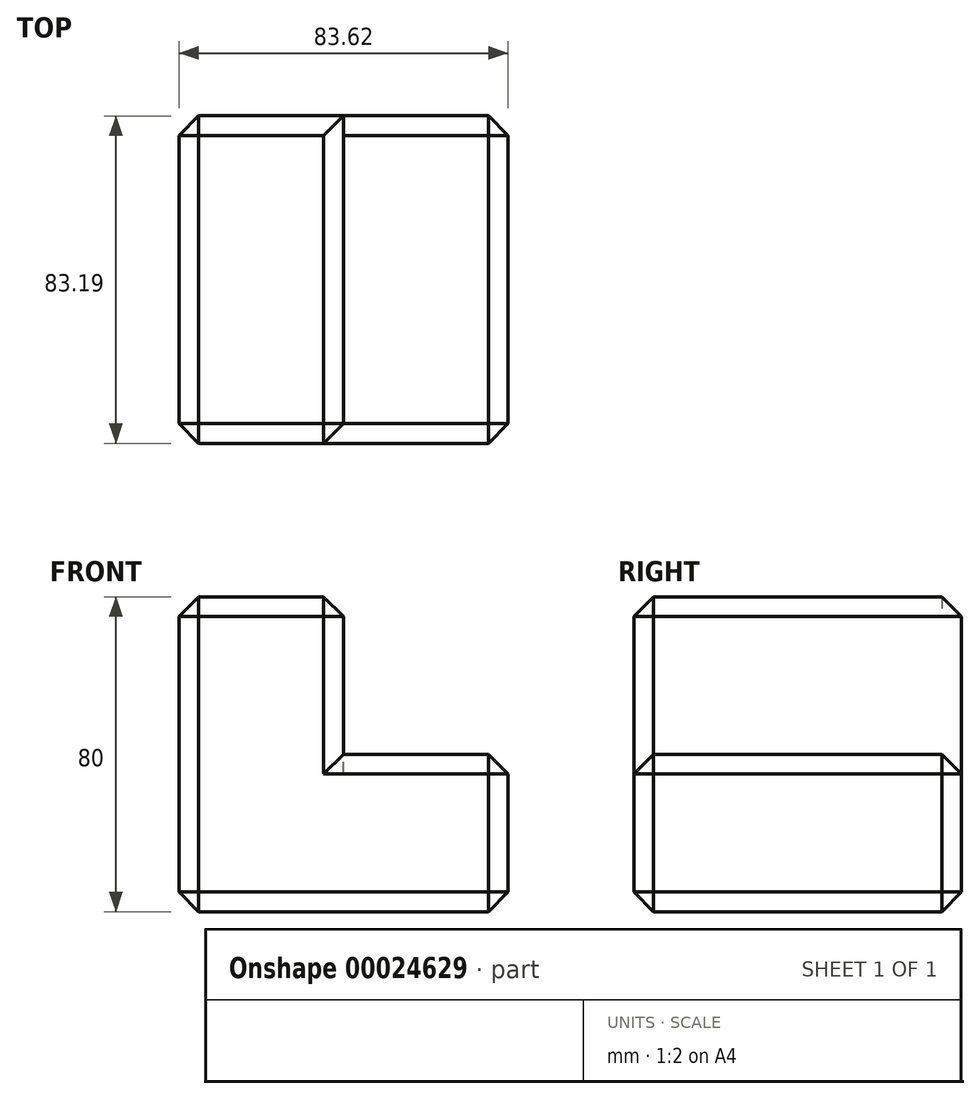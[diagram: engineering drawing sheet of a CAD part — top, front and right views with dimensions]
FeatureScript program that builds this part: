
annotation { "Feature Type Name" : "Feature", "Feature Type Description" : "" }
export const myFeature = defineFeature(function(context is Context, id is Id, definition is map)
    precondition{}
    {
        {
            var Q0;
            Q0=qCreatedBy(makeId("Top.planeOp"),FACE);
            var sketch = newSketch(context, id + "F0", { "sketchPlane" : qUnion([Q0])});
            skLineSegment(sketch, "E0.bottom", {"start": v(-59.13, -45.93) * mm, "end": v(24.5, -45.93) * mm});
            skLineSegment(sketch, "E0.top", {"start": v(-59.13, 37.26) * mm, "end": v(24.5, 37.26) * mm});
            skLineSegment(sketch, "E0.left", {"start": v(-59.13, -45.93) * mm, "end": v(-59.13, 37.26) * mm});
            skLineSegment(sketch, "E0.right", {"start": v(24.5, -45.93) * mm, "end": v(24.5, 37.26) * mm});
            skSolve(sketch);
        }
        {
            var Q0;
            Q0=makeQuery(id+"F0.imprint","IMPRINT",FACE,{"disambiguationData":[TD([[makeQuery(id+"F0.imprint","IMPRINT",EDGE,{"derivedFrom":sQuery(id+"F0.wireOp",EDGE,"E0.bottom")}),1.0]])]});
            extrude(context, id + "F1", {"entities" : qUnion([Q0]), "depth" : 40 * mm});
        }
        {
            var Q0;
            Q0=makeQuery(id+"F1.opExtrude","CAP_FACE",FACE,{"disambiguationData":[OSD([sQuery(id+"F0.wireOp",EDGE,"E0.bottom"),sQuery(id+"F0.wireOp",EDGE,"E0.top"),sQuery(id+"F0.wireOp",EDGE,"E0.left"),sQuery(id+"F0.wireOp",EDGE,"E0.right")])],"isStart":false});
            var sketch = newSketch(context, id + "F2", { "sketchPlane" : qUnion([Q0])});
            skLineSegment(sketch, "E1", {"start": v(-17.32, 37.26) * mm, "end": v(-17.32, -45.93) * mm});
            skSolve(sketch);
        }
        {
            var Q0;
            {var subQ1=sQuery(id+"F2.wireOp",EDGE,"E1");Q0=makeQuery(id+"F2.imprint","IMPRINT",FACE,{"disambiguationData":[TD([[makeQuery(id+"F2.imprint","IMPRINT",EDGE,{"derivedFrom":subQ1}),-1.0]])]});}
            extrude(context, id + "F3", {"entities" : qUnion([Q0]), "operationType" : NewBodyOperationType.ADD, "depth" : 40 * mm});
        }
        {
            var Q0;
            Q0=makeQuery(id+"F3.opExtrude","CAP_EDGE",EDGE,{"disambiguationData":[OSD([sQuery(id+"F0.wireOp",EDGE,"E0.bottom")])],"isStart":false});
            var Q1;
            {var subQ0=sQuery(id+"F0.wireOp",EDGE,"E0.bottom");Q1=makeQuery(id+"F3.boolean.opBoolean","MERGE",FACE,{"derivedFrom":[makeQuery(id+"F1.opExtrude","SWEPT_FACE",FACE,{"disambiguationData":[OSD([subQ0])]}),makeQuery(id+"F3.opExtrude","SWEPT_FACE",FACE,{"disambiguationData":[OSD([subQ0])]})]});}
            var Q2;
            Q2=makeQuery(id+"F3.opExtrude","CAP_EDGE",EDGE,{"disambiguationData":[OSD([sQuery(id+"F2.wireOp",EDGE,"E1")])],"isStart":false});
            var Q3;
            Q3=makeQuery(id+"F3.opExtrude","CAP_EDGE",EDGE,{"disambiguationData":[OSD([sQuery(id+"F2.wireOp",EDGE,"E1")])],"isStart":true});
            var Q4;
            Q4=makeQuery(id+"F1.opExtrude","CAP_EDGE",EDGE,{"disambiguationData":[OSD([sQuery(id+"F0.wireOp",EDGE,"E0.right")])],"isStart":false});
            var Q5;
            Q5=makeQuery(id+"F1.opExtrude","CAP_EDGE",EDGE,{"disambiguationData":[OSD([sQuery(id+"F0.wireOp",EDGE,"E0.right")])],"isStart":true});
            var Q6;
            Q6=makeQuery(id+"F3.opExtrude","CAP_EDGE",EDGE,{"disambiguationData":[OSD([sQuery(id+"F0.wireOp",EDGE,"E0.left")])],"isStart":false});
            var Q7;
            Q7=makeQuery(id+"F1.opExtrude","CAP_EDGE",EDGE,{"disambiguationData":[OSD([sQuery(id+"F0.wireOp",EDGE,"E0.top")])],"isStart":false});
            var Q8;
            Q8=makeQuery(id+"F1.opExtrude","SWEPT_EDGE",EDGE,{"disambiguationData":[OSD([sQuery(id+"F0.wireOp",EDGE,"E0.top"),sQuery(id+"F0.wireOp",EDGE,"E0.right")])]});
            var Q9;
            Q9=makeQuery(id+"F1.opExtrude","CAP_EDGE",EDGE,{"disambiguationData":[OSD([sQuery(id+"F0.wireOp",EDGE,"E0.top")])],"isStart":true});
            var Q10;
            Q10=makeQuery(id+"F3.opExtrude","CAP_EDGE",EDGE,{"disambiguationData":[OSD([sQuery(id+"F0.wireOp",EDGE,"E0.top")])],"isStart":false});
            var Q11;
            {var subQ0=sQuery(id+"F0.wireOp",EDGE,"E0.top");var subQ1=sQuery(id+"F0.wireOp",EDGE,"E0.left");Q11=makeQuery(id+"F3.boolean.opBoolean","MERGE",EDGE,{"derivedFrom":[makeQuery(id+"F1.opExtrude","SWEPT_EDGE",EDGE,{"disambiguationData":[OSD([subQ0,subQ1])]}),makeQuery(id+"F3.opExtrude","SWEPT_EDGE",EDGE,{"disambiguationData":[OSD([subQ0,subQ1])]})]});}
            var Q12;
            Q12=makeQuery(id+"F1.opExtrude","CAP_EDGE",EDGE,{"disambiguationData":[OSD([sQuery(id+"F0.wireOp",EDGE,"E0.left")])],"isStart":true});
            chamfer(context, id + "F4", {"entities" : qUnion([Q0, Q1, Q2, Q3, Q4, Q5, Q6, Q7, Q8, Q9, Q10, Q11, Q12]), "width" : 5 * mm, "tangentPropagation" : true});
        }
    });
